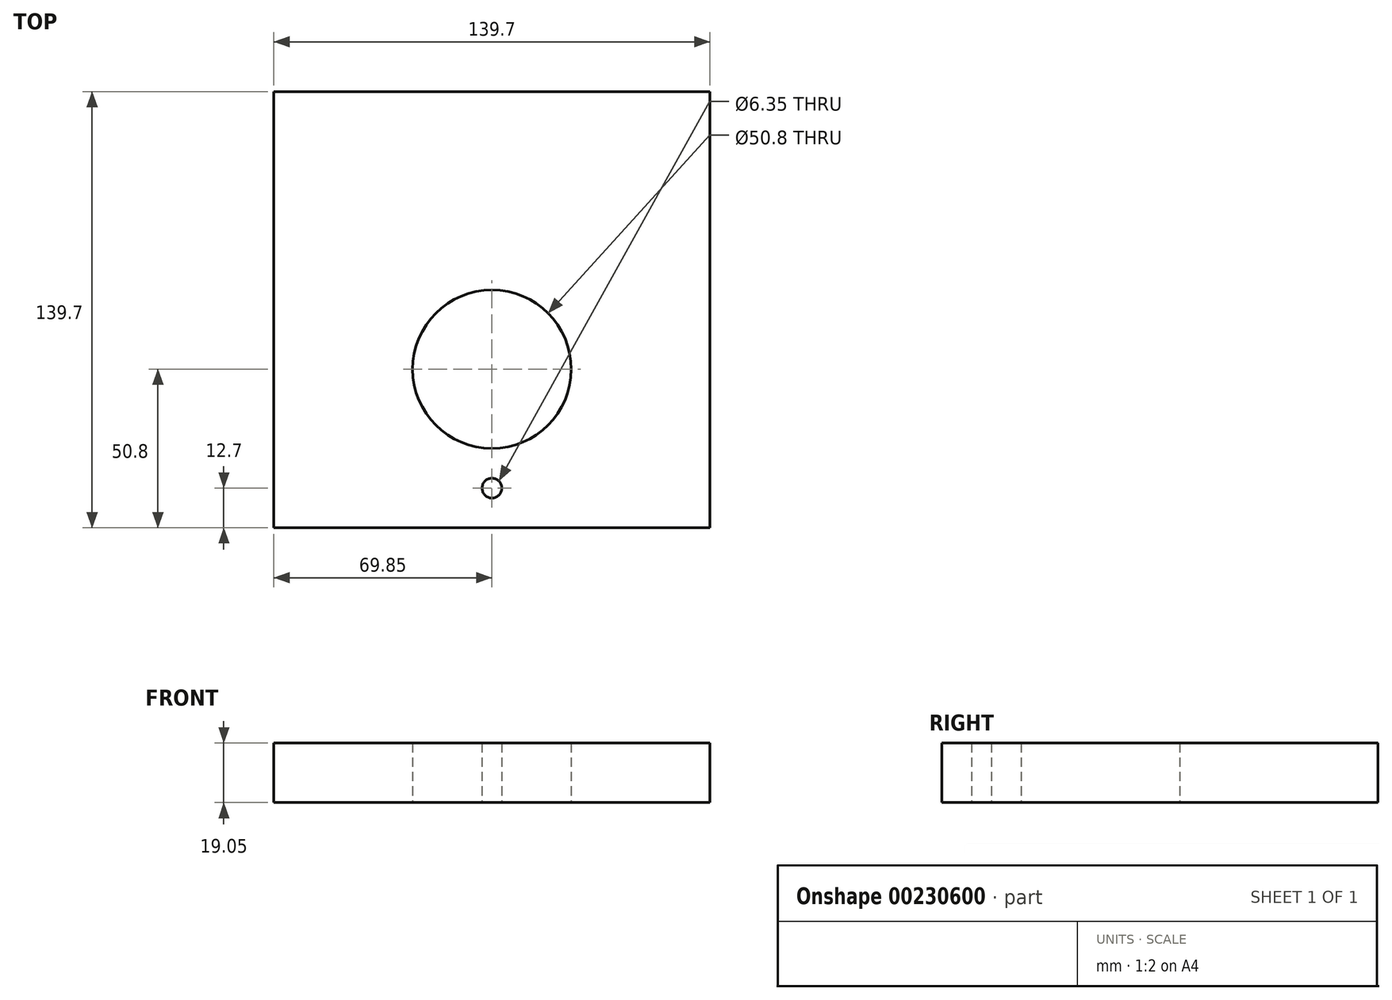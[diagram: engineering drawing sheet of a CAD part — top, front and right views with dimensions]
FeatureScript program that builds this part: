
annotation { "Feature Type Name" : "Feature", "Feature Type Description" : "" }
export const myFeature = defineFeature(function(context is Context, id is Id, definition is map)
    precondition{}
    {
        {
            var Q0;
            Q0=qCreatedBy(makeId("Top.planeOp"),FACE);
            var sketch = newSketch(context, id + "F0", { "sketchPlane" : qUnion([Q0])});
            skLineSegment(sketch, "E0.bottom", {"start": v(-69.85, 69.85) * mm, "end": v(69.85, 69.85) * mm});
            skLineSegment(sketch, "E0.top", {"start": v(-69.85, -69.85) * mm, "end": v(69.85, -69.85) * mm});
            skLineSegment(sketch, "E0.left", {"start": v(-69.85, 69.85) * mm, "end": v(-69.85, -69.85) * mm});
            skLineSegment(sketch, "E0.right", {"start": v(69.85, 69.85) * mm, "end": v(69.85, -69.85) * mm});
            skPoint(sketch, "E0.middle", {"position": v(0, 0) * mm});
            skLineSegment(sketch, "E1", {"start": v(0, -69.85) * mm, "end": v(0, -57.15) * mm});
            skPoint(sketch, "E1.endSnap0", {"position": v(0, -69.85) * mm});
            skLineSegment(sketch, "E2", {"start": v(0, -57.15) * mm, "end": v(0, -19.05) * mm});
            skCircle(sketch, "E3", {"center": v(0, -57.15) * mm, "radius": 3.18 * mm});
            skCircle(sketch, "E4", {"center": v(0, -19.05) * mm, "radius": 25.4 * mm});
            skSolve(sketch);
        }
        {
            var Q0;
            Q0=makeQuery(id+"F0.imprint","IMPRINT",FACE,{"disambiguationData":[TD([[makeQuery(id+"F0.imprint","IMPRINT",EDGE,{"derivedFrom":sQuery(id+"F0.wireOp",EDGE,"E0.bottom")}),-1.0]])]});
            extrude(context, id + "F1", {"entities" : qUnion([Q0]), "depth" : 19.05 * mm});
        }
    });
